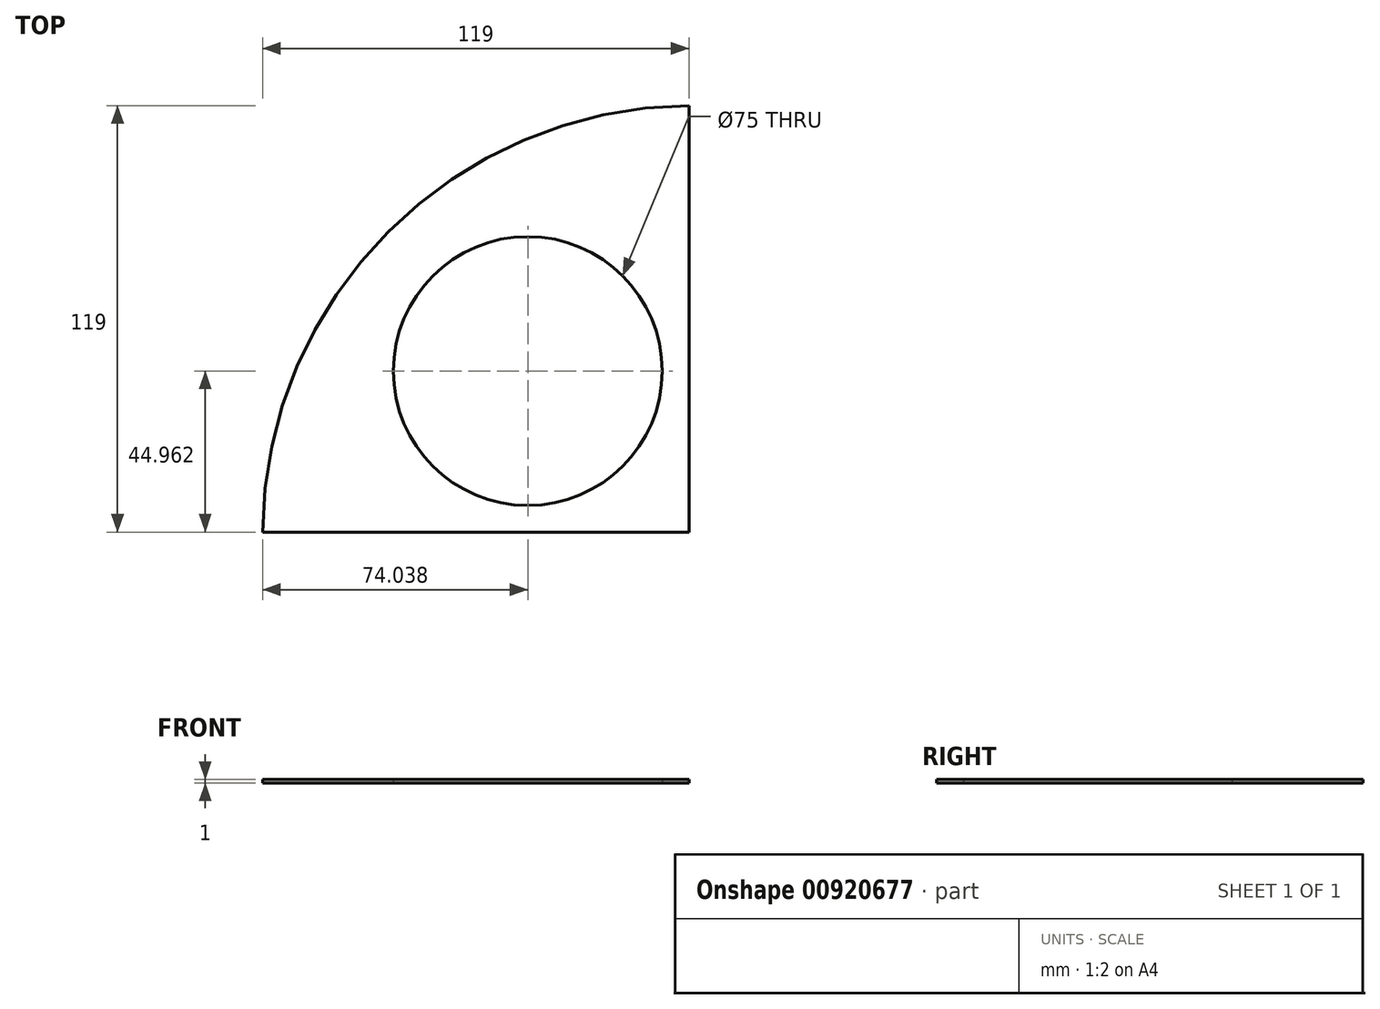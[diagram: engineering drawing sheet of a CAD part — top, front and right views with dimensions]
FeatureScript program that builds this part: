
annotation { "Feature Type Name" : "Feature", "Feature Type Description" : "" }
export const myFeature = defineFeature(function(context is Context, id is Id, definition is map)
    precondition{}
    {
        {
            var Q0;
            Q0=qCreatedBy(makeId("Top.planeOp"),FACE);
            var sketch = newSketch(context, id + "F0", { "sketchPlane" : qUnion([Q0])});
            skCircle(sketch, "E0", {"center": v(0, 0) * mm, "radius": 120 * mm});
            skCircle(sketch, "E1", {"center": v(0, 0) * mm, "radius": 65 * mm, "construction": true});
            skLineSegment(sketch, "E2", {"start": v(0, 0) * mm, "end": v(-107.78, 107.78) * mm, "construction": true});
            skCircle(sketch, "E3", {"center": v(-45.96, 45.96) * mm, "radius": 37.5 * mm});
            skLineSegment(sketch, "E4", {"start": v(0, 0) * mm, "end": v(-120, 0) * mm, "construction": true});
            skLineSegment(sketch, "E5", {"start": v(0, 0) * mm, "end": v(0, 120) * mm, "construction": true});
            skLineSegment(sketch, "E6.0", {"start": v(-1, 1) * mm, "end": v(-120, 1) * mm});
            skLineSegment(sketch, "E6.1", {"start": v(-1, 1) * mm, "end": v(-1, 120) * mm});
            skSolve(sketch);
        }
        {
            var Q0;
            Q0=makeQuery(id+"F0.imprint","IMPRINT",FACE,{"disambiguationData":[TD([[makeQuery(id+"F0.imprint","IMPRINT",EDGE,{"derivedFrom":sQuery(id+"F0.wireOp",EDGE,"E3")}),-1.0]])]});
            extrude(context, id + "F1", {"entities" : qUnion([Q0]), "depth" : 1 * mm, "offsetDistance" : 25 * mm});
        }
    });
